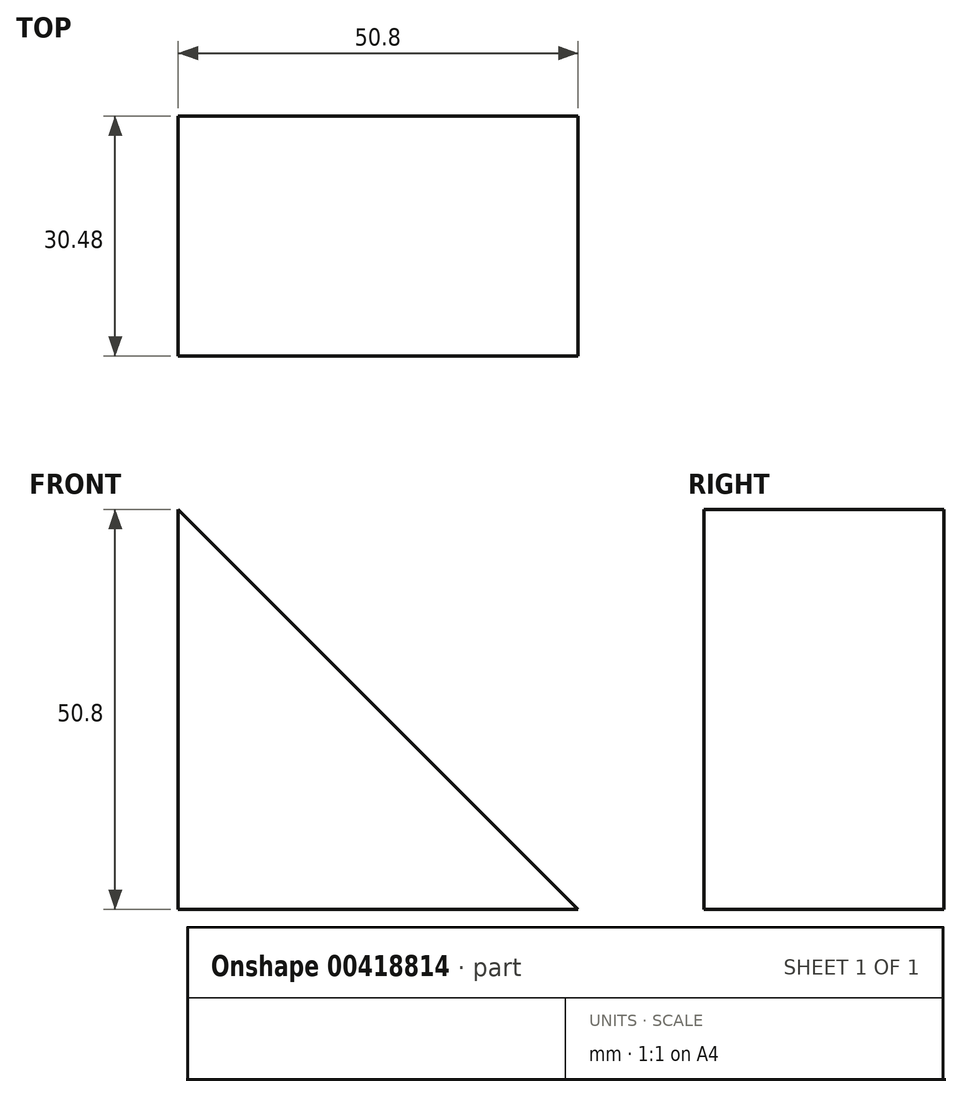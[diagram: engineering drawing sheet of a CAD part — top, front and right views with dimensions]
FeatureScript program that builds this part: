
annotation { "Feature Type Name" : "Feature", "Feature Type Description" : "" }
export const myFeature = defineFeature(function(context is Context, id is Id, definition is map)
    precondition{}
    {
        {
            var Q0;
            Q0=qCreatedBy(makeId("Front.planeOp"),FACE);
            var sketch = newSketch(context, id + "F0", { "sketchPlane" : qUnion([Q0])});
            skLineSegment(sketch, "E0", {"start": v(0, 0) * mm, "end": v(-50.8, 0) * mm});
            skLineSegment(sketch, "E1", {"start": v(-50.8, 0) * mm, "end": v(-50.8, 50.8) * mm});
            skLineSegment(sketch, "E2", {"start": v(-50.8, 50.8) * mm, "end": v(0, 0) * mm});
            skSolve(sketch);
        }
        {
            var Q0;
            Q0=makeQuery(id+"F0.imprint","IMPRINT",FACE,{"disambiguationData":[TD([[makeQuery(id+"F0.imprint","IMPRINT",EDGE,{"derivedFrom":sQuery(id+"F0.wireOp",EDGE,"E0")}),-1.0]])]});
            extrude(context, id + "F1", {"entities" : qUnion([Q0]), "depth" : 30.48 * mm});
        }
    });
